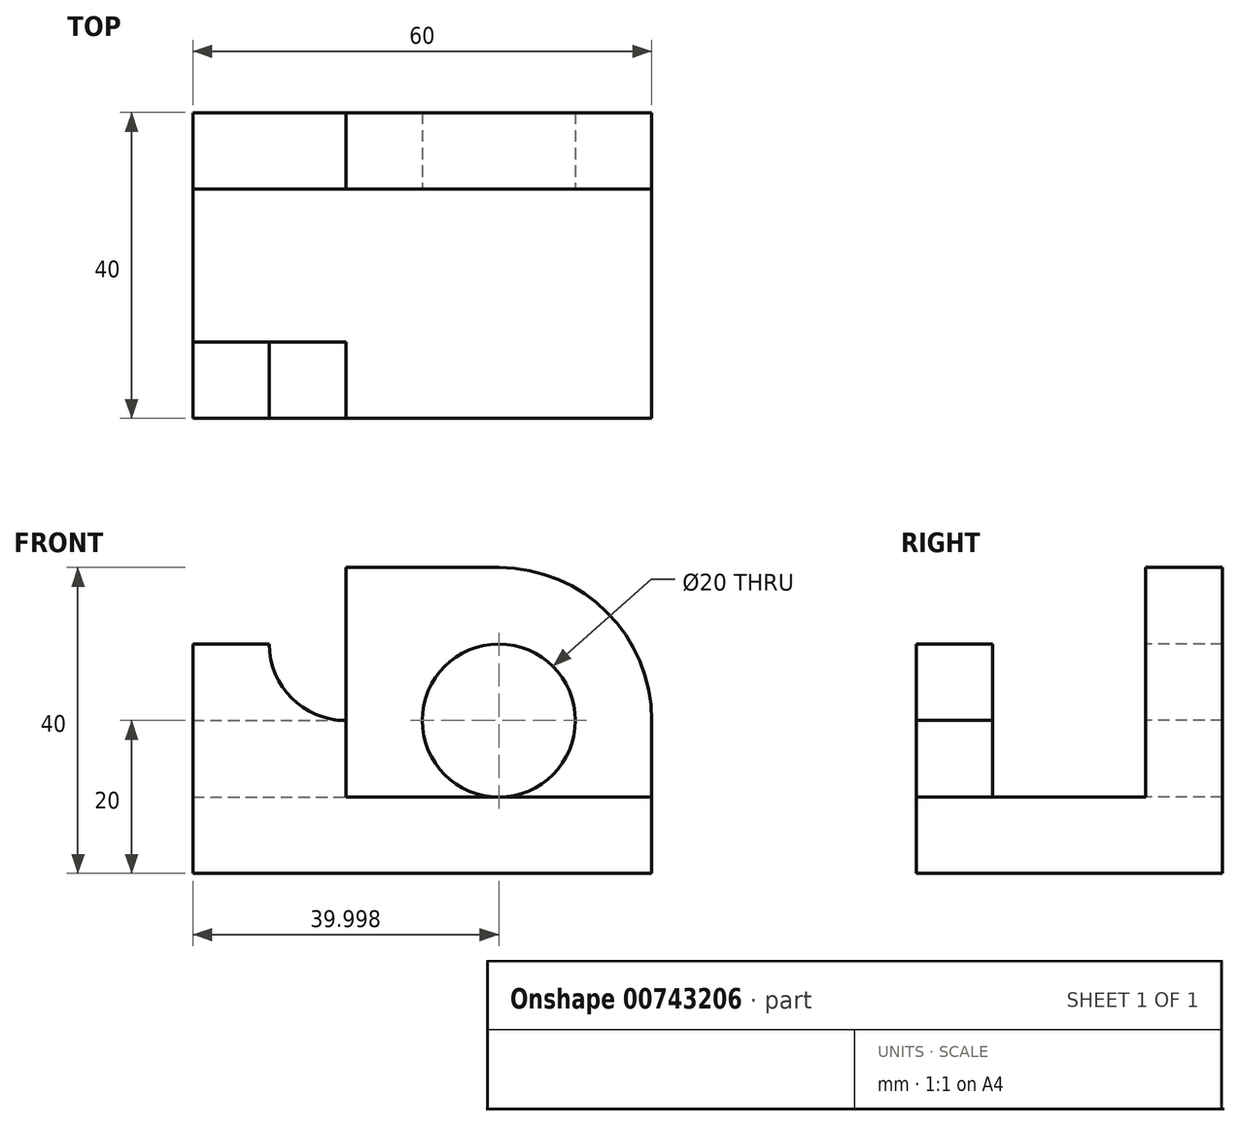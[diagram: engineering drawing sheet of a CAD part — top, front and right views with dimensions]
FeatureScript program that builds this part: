
annotation { "Feature Type Name" : "Feature", "Feature Type Description" : "" }
export const myFeature = defineFeature(function(context is Context, id is Id, definition is map)
    precondition{}
    {
        {
            var Q0;
            Q0=qCreatedBy(makeId("Top.planeOp"),FACE);
            var sketch = newSketch(context, id + "F0", { "sketchPlane" : qUnion([Q0])});
            skLineSegment(sketch, "E0.bottom", {"start": v(-32.2, 29.29) * mm, "end": v(27.8, 29.29) * mm});
            skLineSegment(sketch, "E0.top", {"start": v(-32.2, -10.71) * mm, "end": v(27.8, -10.71) * mm});
            skLineSegment(sketch, "E0.left", {"start": v(-32.2, 29.29) * mm, "end": v(-32.2, -10.71) * mm});
            skLineSegment(sketch, "E0.right", {"start": v(27.8, 29.29) * mm, "end": v(27.8, -10.71) * mm});
            skSolve(sketch);
        }
        {
            var Q0;
            Q0=makeQuery(id+"F0.imprint","IMPRINT",FACE,{"disambiguationData":[TD([[makeQuery(id+"F0.imprint","IMPRINT",EDGE,{"derivedFrom":sQuery(id+"F0.wireOp",EDGE,"E0.bottom")}),-1.0]])]});
            extrude(context, id + "F1", {"entities" : qUnion([Q0]), "depth" : 10 * mm, "offsetDistance" : 25.4 * mm});
        }
        {
            var Q0;
            Q0=makeQuery(id+"F1.opExtrude","CAP_FACE",FACE,{"disambiguationData":[OSD([sQuery(id+"F0.wireOp",EDGE,"E0.bottom"),sQuery(id+"F0.wireOp",EDGE,"E0.top"),sQuery(id+"F0.wireOp",EDGE,"E0.left"),sQuery(id+"F0.wireOp",EDGE,"E0.right")])],"isStart":false});
            var sketch = newSketch(context, id + "F2", { "sketchPlane" : qUnion([Q0])});
            skLineSegment(sketch, "E1.bottom", {"start": v(-32.2, 29.29) * mm, "end": v(27.8, 29.29) * mm});
            skLineSegment(sketch, "E1.top", {"start": v(-32.2, 19.29) * mm, "end": v(27.8, 19.29) * mm});
            skLineSegment(sketch, "E1.left", {"start": v(-32.2, 29.29) * mm, "end": v(-32.2, 19.29) * mm});
            skLineSegment(sketch, "E1.right", {"start": v(27.8, 29.29) * mm, "end": v(27.8, 19.29) * mm});
            skSolve(sketch);
        }
        {
            var Q0;
            Q0=makeQuery(id+"F2.imprint","IMPRINT",FACE,{"disambiguationData":[TD([[makeQuery(id+"F2.imprint","IMPRINT",EDGE,{"derivedFrom":sQuery(id+"F2.wireOp",EDGE,"E1.bottom")}),-1.0]])]});
            extrude(context, id + "F3", {"entities" : qUnion([Q0]), "operationType" : NewBodyOperationType.ADD, "depth" : 30 * mm, "offsetDistance" : 25.4 * mm});
        }
        {
            var Q0;
            Q0=makeQuery(id+"F3.opExtrude","CAP_FACE",FACE,{"disambiguationData":[OSD([sQuery(id+"F2.wireOp",EDGE,"E1.bottom"),sQuery(id+"F2.wireOp",EDGE,"E1.top"),sQuery(id+"F2.wireOp",EDGE,"E1.left"),sQuery(id+"F2.wireOp",EDGE,"E1.right")])],"isStart":false});
            var sketch = newSketch(context, id + "F4", { "sketchPlane" : qUnion([Q0])});
            skLineSegment(sketch, "E2.bottom", {"start": v(-32.2, 29.29) * mm, "end": v(-12.2, 29.29) * mm});
            skLineSegment(sketch, "E2.top", {"start": v(-32.2, 19.29) * mm, "end": v(-12.2, 19.29) * mm});
            skLineSegment(sketch, "E2.left", {"start": v(-32.2, 29.29) * mm, "end": v(-32.2, 19.29) * mm});
            skLineSegment(sketch, "E2.right", {"start": v(-12.2, 29.29) * mm, "end": v(-12.2, 19.29) * mm});
            skSolve(sketch);
        }
        {
            var Q0;
            Q0=makeQuery(id+"F4.imprint","IMPRINT",FACE,{"disambiguationData":[TD([[makeQuery(id+"F4.imprint","IMPRINT",EDGE,{"derivedFrom":sQuery(id+"F4.wireOp",EDGE,"E2.bottom")}),-1.0]])]});
            extrude(context, id + "F5", {"entities" : qUnion([Q0]), "operationType" : NewBodyOperationType.REMOVE, "oppositeDirection" : true, "depth" : 20 * mm, "offsetDistance" : 25.4 * mm});
        }
        {
            var Q0;
            Q0=makeQuery(id+"F5.boolean.opBoolean","COPY",EDGE,{"derivedFrom":makeQuery(id+"F5.opExtrude","CAP_EDGE",EDGE,{"disambiguationData":[OSD([sQuery(id+"F4.wireOp",EDGE,"E2.right")])],"isStart":true})});
            var Q1;
            Q1=makeQuery(id+"F3.opExtrude","CAP_EDGE",EDGE,{"disambiguationData":[OSD([sQuery(id+"F2.wireOp",EDGE,"E1.right")])],"isStart":false});
            fillet(context, id + "F6", {"entities" : qUnion([Q0, Q1]), "radius" : 20 * mm, "tangentPropagation" : true, "allowEdgeOverflow" : false});
        }
        {
            var Q0;
            Q0=makeQuery(id+"F3.opExtrude","SWEPT_FACE",FACE,{"disambiguationData":[OSD([sQuery(id+"F2.wireOp",EDGE,"E1.top")])]});
            var sketch = newSketch(context, id + "F7", { "sketchPlane" : qUnion([Q0])});
            skCircle(sketch, "E3", {"center": v(7.8, 20) * mm, "radius": 10 * mm});
            skSolve(sketch);
        }
        {
            var Q0;
            Q0=makeQuery(id+"F7.imprint","IMPRINT",FACE,{"disambiguationData":[TD([[makeQuery(id+"F7.imprint","IMPRINT",EDGE,{"derivedFrom":sQuery(id+"F7.wireOp",EDGE,"E3")}),1.0]])]});
            extrude(context, id + "F8", {"entities" : qUnion([Q0]), "operationType" : NewBodyOperationType.REMOVE, "oppositeDirection" : true, "depth" : 10 * mm, "offsetDistance" : 25.4 * mm});
        }
        {
            var Q0;
            Q0=makeQuery(id+"F1.opExtrude","CAP_FACE",FACE,{"disambiguationData":[OSD([sQuery(id+"F0.wireOp",EDGE,"E0.bottom"),sQuery(id+"F0.wireOp",EDGE,"E0.top"),sQuery(id+"F0.wireOp",EDGE,"E0.left"),sQuery(id+"F0.wireOp",EDGE,"E0.right")])],"isStart":false});
            var sketch = newSketch(context, id + "F9", { "sketchPlane" : qUnion([Q0])});
            skLineSegment(sketch, "E4.bottom", {"start": v(-32.2, -10.71) * mm, "end": v(-12.2, -10.71) * mm});
            skLineSegment(sketch, "E4.top", {"start": v(-32.2, -0.71) * mm, "end": v(-12.2, -0.71) * mm});
            skLineSegment(sketch, "E4.left", {"start": v(-32.2, -10.71) * mm, "end": v(-32.2, -0.71) * mm});
            skLineSegment(sketch, "E4.right", {"start": v(-12.2, -10.71) * mm, "end": v(-12.2, -0.71) * mm});
            skSolve(sketch);
        }
        {
            var Q0;
            Q0=makeQuery(id+"F9.imprint","IMPRINT",FACE,{"disambiguationData":[TD([[makeQuery(id+"F9.imprint","IMPRINT",EDGE,{"derivedFrom":sQuery(id+"F9.wireOp",EDGE,"E4.bottom")}),1.0]])]});
            extrude(context, id + "F10", {"entities" : qUnion([Q0]), "operationType" : NewBodyOperationType.ADD, "depth" : 20 * mm, "offsetDistance" : 25.4 * mm});
        }
        {
            var Q0;
            Q0=makeQuery(id+"F10.boolean.opBoolean","MERGE",FACE,{"derivedFrom":[makeQuery(id+"F1.opExtrude","SWEPT_FACE",FACE,{"disambiguationData":[OSD([sQuery(id+"F0.wireOp",EDGE,"E0.top")])]}),makeQuery(id+"F10.opExtrude","SWEPT_FACE",FACE,{"disambiguationData":[OSD([sQuery(id+"F9.wireOp",EDGE,"E4.bottom")])]})]});
            var sketch = newSketch(context, id + "F11", { "sketchPlane" : qUnion([Q0])});
            skArc(sketch, "E5", {"start": v(-22.2, 30) * mm, "mid": v(-19.27, 22.93) * mm, "end": v(-12.2, 20) * mm});
            skLineSegment(sketch, "E6", {"start": v(-12.2, 30) * mm, "end": v(-22.2, 30) * mm});
            skLineSegment(sketch, "E7", {"start": v(-12.2, 20) * mm, "end": v(-12.2, 30) * mm});
            skSolve(sketch);
        }
        {
            var Q0;
            Q0=makeQuery(id+"F11.imprint","IMPRINT",FACE,{"disambiguationData":[TD([[makeQuery(id+"F11.imprint","IMPRINT",EDGE,{"derivedFrom":sQuery(id+"F11.wireOp",EDGE,"E5")}),1.0]])]});
            extrude(context, id + "F12", {"entities" : qUnion([Q0]), "operationType" : NewBodyOperationType.REMOVE, "oppositeDirection" : true, "depth" : 10 * mm, "offsetDistance" : 25.4 * mm});
        }
    });
